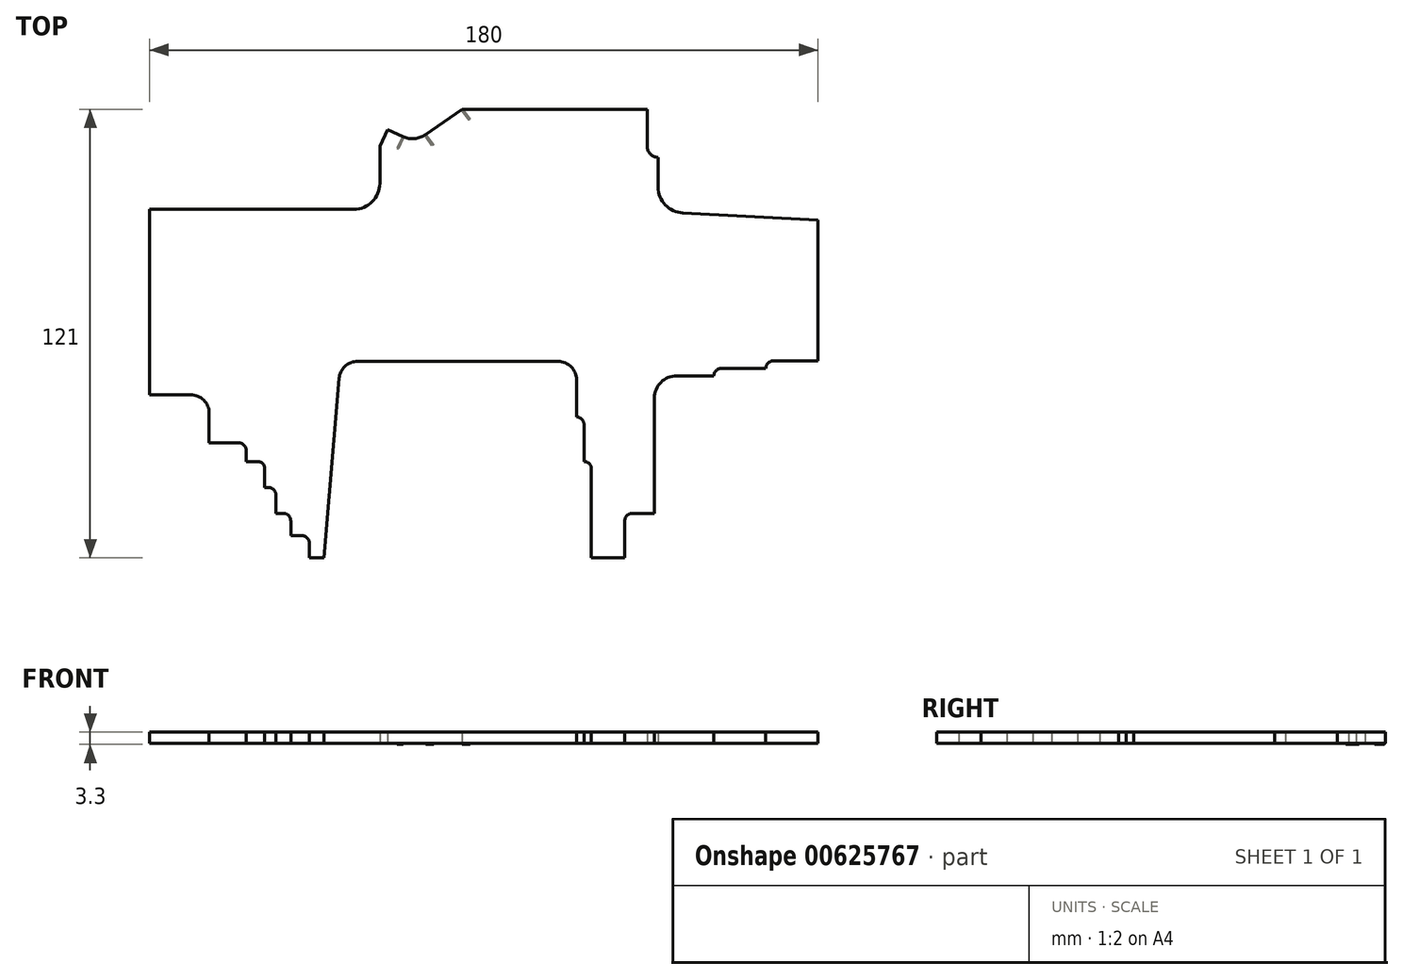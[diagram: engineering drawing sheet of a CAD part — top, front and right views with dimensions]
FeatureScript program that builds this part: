
annotation { "Feature Type Name" : "Feature", "Feature Type Description" : "" }
export const myFeature = defineFeature(function(context is Context, id is Id, definition is map)
    precondition{}
    {
        {
            var Q0;
            Q0=qCreatedBy(makeId("Top.planeOp"),FACE);
            var sketch = newSketch(context, id + "F0", { "sketchPlane" : qUnion([Q0])});
            skLineSegment(sketch, "E0", {"start": v(0, 0) * mm, "end": v(-9, 0) * mm});
            skLineSegment(sketch, "E1", {"start": v(-9, 0) * mm, "end": v(-9, 24) * mm});
            skLineSegment(sketch, "E2", {"start": v(-11, 26) * mm, "end": v(-11, 26) * mm});
            skLineSegment(sketch, "E3", {"start": v(-11, 26) * mm, "end": v(-11, 36) * mm});
            skLineSegment(sketch, "E4", {"start": v(-13, 38) * mm, "end": v(-13, 38) * mm});
            skLineSegment(sketch, "E5", {"start": v(-13, 38) * mm, "end": v(-13, 48) * mm});
            skLineSegment(sketch, "E6", {"start": v(-18, 53) * mm, "end": v(-72, 53) * mm});
            skPoint(sketch, "E7.visualSharp", {"position": v(-9, 26) * mm});
            skArc(sketch, "E7.filletArc", {"start": v(-9, 24) * mm, "mid": v(-9.59, 25.41) * mm, "end": v(-11, 26) * mm});
            skPoint(sketch, "E8.visualSharp", {"position": v(-11, 38) * mm});
            skArc(sketch, "E8.filletArc", {"start": v(-11, 36) * mm, "mid": v(-11.59, 37.41) * mm, "end": v(-13, 38) * mm});
            skPoint(sketch, "E9.visualSharp", {"position": v(-13, 53) * mm});
            skArc(sketch, "E9.filletArc", {"start": v(-13, 48) * mm, "mid": v(-14.46, 51.54) * mm, "end": v(-18, 53) * mm});
            skLineSegment(sketch, "E10", {"start": v(-76.98, 48.41) * mm, "end": v(-81, 0) * mm});
            skLineSegment(sketch, "E11", {"start": v(-81, 0) * mm, "end": v(-85, 0) * mm});
            skLineSegment(sketch, "E12", {"start": v(-85, 0) * mm, "end": v(-85, 4) * mm});
            skLineSegment(sketch, "E13", {"start": v(-87, 6) * mm, "end": v(-90, 6) * mm});
            skLineSegment(sketch, "E14", {"start": v(-90, 6) * mm, "end": v(-90, 10) * mm});
            skLineSegment(sketch, "E15", {"start": v(-92, 12) * mm, "end": v(-94, 12) * mm});
            skLineSegment(sketch, "E16", {"start": v(-94, 12) * mm, "end": v(-94, 17) * mm});
            skLineSegment(sketch, "E17", {"start": v(-96, 19) * mm, "end": v(-97, 19) * mm});
            skLineSegment(sketch, "E18", {"start": v(-97, 19) * mm, "end": v(-97, 24) * mm});
            skLineSegment(sketch, "E19", {"start": v(-99, 26) * mm, "end": v(-102, 26) * mm});
            skLineSegment(sketch, "E20", {"start": v(-102, 26) * mm, "end": v(-102, 29) * mm});
            skLineSegment(sketch, "E21", {"start": v(-104, 31) * mm, "end": v(-112, 31) * mm});
            skLineSegment(sketch, "E22", {"start": v(-112, 31) * mm, "end": v(-112, 39) * mm});
            skLineSegment(sketch, "E23", {"start": v(-117, 44) * mm, "end": v(-128, 44) * mm});
            skLineSegment(sketch, "E24", {"start": v(-128, 44) * mm, "end": v(-128, 94) * mm});
            skPoint(sketch, "E25.visualSharp", {"position": v(-112, 44) * mm});
            skArc(sketch, "E25.filletArc", {"start": v(-112, 39) * mm, "mid": v(-113.46, 42.54) * mm, "end": v(-117, 44) * mm});
            skPoint(sketch, "E26.visualSharp", {"position": v(-102, 31) * mm});
            skArc(sketch, "E26.filletArc", {"start": v(-102, 29) * mm, "mid": v(-102.59, 30.41) * mm, "end": v(-104, 31) * mm});
            skPoint(sketch, "E27.visualSharp", {"position": v(-97, 26) * mm});
            skArc(sketch, "E27.filletArc", {"start": v(-97, 24) * mm, "mid": v(-97.59, 25.41) * mm, "end": v(-99, 26) * mm});
            skPoint(sketch, "E28.visualSharp", {"position": v(-94, 19) * mm});
            skArc(sketch, "E28.filletArc", {"start": v(-94, 17) * mm, "mid": v(-94.59, 18.41) * mm, "end": v(-96, 19) * mm});
            skPoint(sketch, "E29.visualSharp", {"position": v(-90, 12) * mm});
            skArc(sketch, "E29.filletArc", {"start": v(-90, 10) * mm, "mid": v(-90.59, 11.41) * mm, "end": v(-92, 12) * mm});
            skPoint(sketch, "E30.visualSharp", {"position": v(-85, 6) * mm});
            skArc(sketch, "E30.filletArc", {"start": v(-85, 4) * mm, "mid": v(-85.59, 5.41) * mm, "end": v(-87, 6) * mm});
            skPoint(sketch, "E31.visualSharp", {"position": v(-76.6, 53) * mm});
            skArc(sketch, "E31.filletArc", {"start": v(-72, 53) * mm, "mid": v(-75.38, 51.68) * mm, "end": v(-76.98, 48.41) * mm});
            skLineSegment(sketch, "E32", {"start": v(-76.98, 48.41) * mm, "end": v(-76.98, 22.2) * mm, "construction": true});
            skLineSegment(sketch, "E33", {"start": v(-128, 94) * mm, "end": v(-73, 94) * mm});
            skLineSegment(sketch, "E34", {"start": v(-66, 101) * mm, "end": v(-66, 111) * mm});
            skPoint(sketch, "E35.visualSharp", {"position": v(-66, 94) * mm});
            skArc(sketch, "E35.filletArc", {"start": v(-73, 94) * mm, "mid": v(-68.05, 96.05) * mm, "end": v(-66, 101) * mm});
            skArc(sketch, "E36", {"start": v(-59.7, 113.58) * mm, "mid": v(-56.64, 113.05) * mm, "end": v(-53.73, 114.11) * mm});
            skLineSegment(sketch, "E37", {"start": v(-53.73, 114.11) * mm, "end": v(-43.9, 121) * mm});
            skLineSegment(sketch, "E38", {"start": v(-43.9, 121) * mm, "end": v(6, 121) * mm});
            skLineSegment(sketch, "E39", {"start": v(6, 121) * mm, "end": v(6, 111) * mm});
            skLineSegment(sketch, "E40", {"start": v(-57.17, 119.02) * mm, "end": v(-59.7, 113.58) * mm, "construction": true});
            skLineSegment(sketch, "E41", {"start": v(-57.17, 119.02) * mm, "end": v(-53.73, 114.11) * mm, "construction": true});
            skLineSegment(sketch, "E42", {"start": v(-66, 111) * mm, "end": v(-63.89, 115.53) * mm});
            skLineSegment(sketch, "E43", {"start": v(-63.89, 115.53) * mm, "end": v(-59.7, 113.58) * mm});
            skLineSegment(sketch, "E44", {"start": v(9, 108) * mm, "end": v(9, 108) * mm});
            skLineSegment(sketch, "E45", {"start": v(9, 108) * mm, "end": v(9, 100) * mm});
            skLineSegment(sketch, "E46", {"start": v(15.63, 93) * mm, "end": v(52, 91.1) * mm});
            skPoint(sketch, "E47.visualSharp", {"position": v(6, 108) * mm});
            skArc(sketch, "E47.filletArc", {"start": v(6, 111) * mm, "mid": v(6.88, 108.88) * mm, "end": v(9, 108) * mm});
            skPoint(sketch, "E48.visualSharp", {"position": v(9, 93.35) * mm});
            skArc(sketch, "E48.filletArc", {"start": v(9, 100) * mm, "mid": v(10.92, 95.17) * mm, "end": v(15.63, 93) * mm});
            skLineSegment(sketch, "E49", {"start": v(15.63, 93) * mm, "end": v(37, 93) * mm, "construction": true});
            skLineSegment(sketch, "E50", {"start": v(52, 91.1) * mm, "end": v(52, 53.1) * mm});
            skLineSegment(sketch, "E51", {"start": v(52, 53.1) * mm, "end": v(40, 53.1) * mm});
            skLineSegment(sketch, "E52", {"start": v(38, 51.1) * mm, "end": v(38, 51.1) * mm});
            skLineSegment(sketch, "E53", {"start": v(38, 51.1) * mm, "end": v(26, 51.1) * mm});
            skLineSegment(sketch, "E54", {"start": v(24, 49.1) * mm, "end": v(24, 49.1) * mm});
            skLineSegment(sketch, "E55", {"start": v(24, 49.1) * mm, "end": v(14, 49.1) * mm});
            skLineSegment(sketch, "E56", {"start": v(8, 43.1) * mm, "end": v(8, 12) * mm});
            skLineSegment(sketch, "E57", {"start": v(8, 12) * mm, "end": v(2, 12) * mm});
            skLineSegment(sketch, "E58", {"start": v(0, 10) * mm, "end": v(0, 0) * mm});
            skPoint(sketch, "E59.visualSharp", {"position": v(38, 53.1) * mm});
            skArc(sketch, "E59.filletArc", {"start": v(40, 53.1) * mm, "mid": v(38.59, 52.5) * mm, "end": v(38, 51.1) * mm});
            skPoint(sketch, "E60.visualSharp", {"position": v(24, 51.1) * mm});
            skArc(sketch, "E60.filletArc", {"start": v(26, 51.1) * mm, "mid": v(24.59, 50.5) * mm, "end": v(24, 49.1) * mm});
            skPoint(sketch, "E61.visualSharp", {"position": v(8, 49.1) * mm});
            skArc(sketch, "E61.filletArc", {"start": v(14, 49.1) * mm, "mid": v(9.76, 47.34) * mm, "end": v(8, 43.1) * mm});
            skPoint(sketch, "E62.visualSharp", {"position": v(0, 12) * mm});
            skArc(sketch, "E62.filletArc", {"start": v(2, 12) * mm, "mid": v(0.59, 11.41) * mm, "end": v(0, 10) * mm});
            skSolve(sketch);
        }
        {
            var Q0;
            Q0 = qSketchRegion(id + "F0", true);
            extrude(context, id + "F1", {"entities" : qUnion([Q0]), "depth" : 3 * mm, "offsetDistance" : 25 * mm});
        }
        {
            var Q0;
            Q0=makeQuery(id+"F1.opExtrude","CAP_FACE",FACE,{"disambiguationData":[OSD([sQuery(id+"F0.wireOp",EDGE,"E0"),sQuery(id+"F0.wireOp",EDGE,"E1"),sQuery(id+"F0.wireOp",EDGE,"E3"),sQuery(id+"F0.wireOp",EDGE,"E5"),sQuery(id+"F0.wireOp",EDGE,"E6"),sQuery(id+"F0.wireOp",EDGE,"E7.filletArc"),sQuery(id+"F0.wireOp",EDGE,"E8.filletArc"),sQuery(id+"F0.wireOp",EDGE,"E9.filletArc"),sQuery(id+"F0.wireOp",EDGE,"E10"),sQuery(id+"F0.wireOp",EDGE,"E11"),sQuery(id+"F0.wireOp",EDGE,"E12"),sQuery(id+"F0.wireOp",EDGE,"E13"),sQuery(id+"F0.wireOp",EDGE,"E14"),sQuery(id+"F0.wireOp",EDGE,"E15"),sQuery(id+"F0.wireOp",EDGE,"E16"),sQuery(id+"F0.wireOp",EDGE,"E17"),sQuery(id+"F0.wireOp",EDGE,"E18"),sQuery(id+"F0.wireOp",EDGE,"E19"),sQuery(id+"F0.wireOp",EDGE,"E20"),sQuery(id+"F0.wireOp",EDGE,"E21"),sQuery(id+"F0.wireOp",EDGE,"E22"),sQuery(id+"F0.wireOp",EDGE,"E23"),sQuery(id+"F0.wireOp",EDGE,"E24"),sQuery(id+"F0.wireOp",EDGE,"E25.filletArc"),sQuery(id+"F0.wireOp",EDGE,"E26.filletArc"),sQuery(id+"F0.wireOp",EDGE,"E27.filletArc"),sQuery(id+"F0.wireOp",EDGE,"E28.filletArc"),sQuery(id+"F0.wireOp",EDGE,"E29.filletArc"),sQuery(id+"F0.wireOp",EDGE,"E30.filletArc"),sQuery(id+"F0.wireOp",EDGE,"E31.filletArc"),sQuery(id+"F0.wireOp",EDGE,"E33"),sQuery(id+"F0.wireOp",EDGE,"E34"),sQuery(id+"F0.wireOp",EDGE,"E35.filletArc"),sQuery(id+"F0.wireOp",EDGE,"E36"),sQuery(id+"F0.wireOp",EDGE,"E37"),sQuery(id+"F0.wireOp",EDGE,"E38"),sQuery(id+"F0.wireOp",EDGE,"E39"),sQuery(id+"F0.wireOp",EDGE,"E42"),sQuery(id+"F0.wireOp",EDGE,"E43"),sQuery(id+"F0.wireOp",EDGE,"E45"),sQuery(id+"F0.wireOp",EDGE,"E46"),sQuery(id+"F0.wireOp",EDGE,"E47.filletArc"),sQuery(id+"F0.wireOp",EDGE,"E48.filletArc"),sQuery(id+"F0.wireOp",EDGE,"E50"),sQuery(id+"F0.wireOp",EDGE,"E51"),sQuery(id+"F0.wireOp",EDGE,"E53"),sQuery(id+"F0.wireOp",EDGE,"E55"),sQuery(id+"F0.wireOp",EDGE,"E56"),sQuery(id+"F0.wireOp",EDGE,"E57"),sQuery(id+"F0.wireOp",EDGE,"E58"),sQuery(id+"F0.wireOp",EDGE,"E59.filletArc"),sQuery(id+"F0.wireOp",EDGE,"E60.filletArc"),sQuery(id+"F0.wireOp",EDGE,"E61.filletArc"),sQuery(id+"F0.wireOp",EDGE,"E62.filletArc")])],"isStart":true});
            var sketch = newSketch(context, id + "F2", { "sketchPlane" : qUnion([Q0])});
            skLineSegment(sketch, "E63", {"start": v(-59.7, -113.58) * mm, "end": v(-61.4, -109.96) * mm, "construction": true});
            skLineSegment(sketch, "E64", {"start": v(-53.73, -114.11) * mm, "end": v(-51.43, -110.84) * mm, "construction": true});
            skLineSegment(sketch, "E65", {"start": v(-43.9, -121) * mm, "end": v(-41.6, -117.72) * mm, "construction": true});
            skLineSegment(sketch, "E66.bottom", {"start": v(-60.14, -113.24) * mm, "end": v(-61.4, -110.52) * mm});
            skLineSegment(sketch, "E66.top", {"start": v(-59.69, -113.02) * mm, "end": v(-60.95, -110.3) * mm});
            skLineSegment(sketch, "E66.left", {"start": v(-60.14, -113.24) * mm, "end": v(-59.69, -113.02) * mm});
            skLineSegment(sketch, "E66.right", {"start": v(-61.4, -110.52) * mm, "end": v(-60.95, -110.3) * mm});
            skPoint(sketch, "E66.middle", {"position": v(-60.55, -111.77) * mm});
            skLineSegment(sketch, "E67.bottom", {"start": v(-51.51, -111.39) * mm, "end": v(-53.23, -113.84) * mm});
            skLineSegment(sketch, "E67.top", {"start": v(-51.92, -111.1) * mm, "end": v(-53.64, -113.56) * mm});
            skLineSegment(sketch, "E67.left", {"start": v(-51.51, -111.39) * mm, "end": v(-51.92, -111.1) * mm});
            skLineSegment(sketch, "E67.right", {"start": v(-53.23, -113.84) * mm, "end": v(-53.64, -113.56) * mm});
            skPoint(sketch, "E67.middle", {"position": v(-52.58, -112.47) * mm});
            skLineSegment(sketch, "E68.bottom", {"start": v(-43.4, -120.73) * mm, "end": v(-41.69, -118.28) * mm});
            skLineSegment(sketch, "E68.top", {"start": v(-43.82, -120.45) * mm, "end": v(-42.1, -118) * mm});
            skLineSegment(sketch, "E68.left", {"start": v(-43.4, -120.73) * mm, "end": v(-43.82, -120.45) * mm});
            skLineSegment(sketch, "E68.right", {"start": v(-41.69, -118.28) * mm, "end": v(-42.1, -118) * mm});
            skPoint(sketch, "E68.middle", {"position": v(-42.75, -119.36) * mm});
            skSolve(sketch);
        }
        {
            var Q0;
            Q0 = qSketchRegion(id + "F2", true);
            extrude(context, id + "F3", {"entities" : qUnion([Q0]), "operationType" : NewBodyOperationType.ADD, "depth" : 0.3 * mm, "offsetDistance" : 25 * mm});
        }
    });
